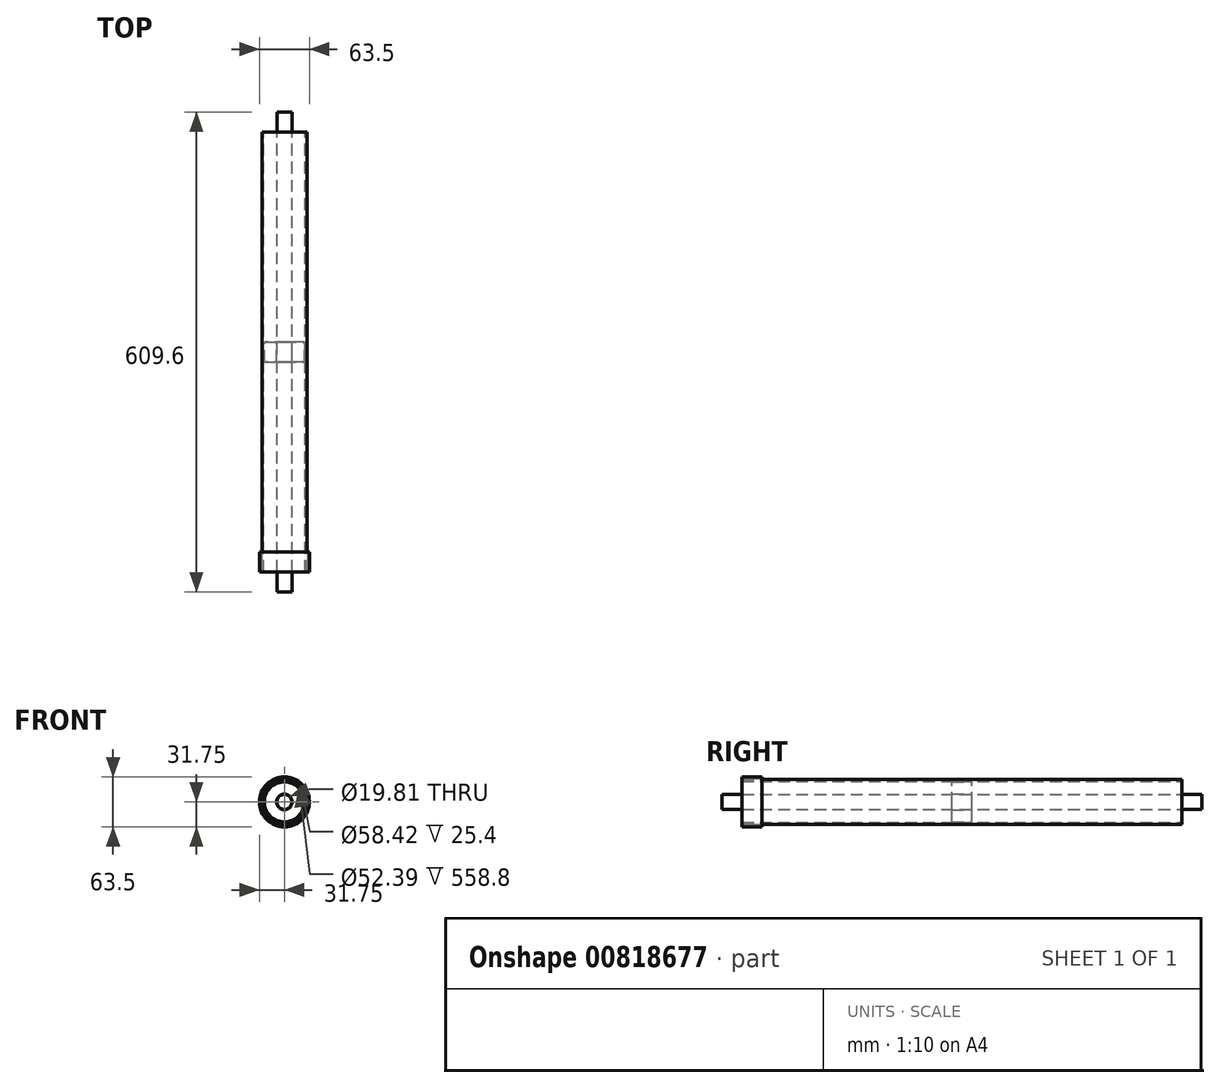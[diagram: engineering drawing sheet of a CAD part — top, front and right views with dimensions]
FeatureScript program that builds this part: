
annotation { "Feature Type Name" : "Feature", "Feature Type Description" : "" }
export const myFeature = defineFeature(function(context is Context, id is Id, definition is map)
    precondition{}
    {
        {
            var Q0;
            Q0=qCreatedBy(makeId("Front.planeOp"),FACE);
            var sketch = newSketch(context, id + "F0", { "sketchPlane" : qUnion([Q0])});
            skCircle(sketch, "E0", {"center": v(0, 0) * mm, "radius": 9.53 * mm});
            skSolve(sketch);
        }
        {
            var Q0;
            Q0 = qSketchRegion(id + "F0", true);
            extrude(context, id + "F1", {"entities" : qUnion([Q0]), "endBound" : BoundingType.SYMMETRIC, "depth" : 609.6 * mm, "offsetDistance" : 25.4 * mm});
        }
        {
            var Q0;
            Q0=qCreatedBy(makeId("Front.planeOp"),FACE);
            var sketch = newSketch(context, id + "F2", { "sketchPlane" : qUnion([Q0])});
            skCircle(sketch, "E1", {"center": v(0, 0) * mm, "radius": 25.4 * mm});
            skCircle(sketch, "E2", {"center": v(0, 0) * mm, "radius": 9.9 * mm});
            skSolve(sketch);
        }
        {
            var Q0;
            Q0 = qSketchRegion(id + "F2", true);
            extrude(context, id + "F3", {"entities" : qUnion([Q0]), "operationType" : NewBodyOperationType.ADD, "endBound" : BoundingType.SYMMETRIC, "depth" : 25.4 * mm, "offsetDistance" : 25.4 * mm});
        }
        {
            var Q0;
            Q0=qCreatedBy(makeId("Front.planeOp"),FACE);
            var sketch = newSketch(context, id + "F4", { "sketchPlane" : qUnion([Q0])});
            skCircle(sketch, "E3", {"center": v(0, 0) * mm, "radius": 26.2 * mm});
            skCircle(sketch, "E4", {"center": v(0, 0) * mm, "radius": 28.58 * mm});
            skSolve(sketch);
        }
        {
            var Q0;
            Q0 = qSketchRegion(id + "F4", true);
            extrude(context, id + "F5", {"entities" : qUnion([Q0]), "endBound" : BoundingType.SYMMETRIC, "depth" : 558.8 * mm, "offsetDistance" : 25.4 * mm});
        }
        {
            var Q0;
            Q0=makeQuery(id+"F5.opExtrude","CAP_FACE",FACE,{"disambiguationData":[OSD([sQuery(id+"F4.wireOp",EDGE,"E3"),sQuery(id+"F4.wireOp",EDGE,"E4")])],"isStart":false});
            var sketch = newSketch(context, id + "F6", { "sketchPlane" : qUnion([Q0])});
            skCircle(sketch, "E5", {"center": v(0, 0) * mm, "radius": 31.75 * mm});
            skCircle(sketch, "E6", {"center": v(0, 0) * mm, "radius": 10.16 * mm});
            skCircle(sketch, "E7", {"center": v(0, 0) * mm, "radius": 29.21 * mm});
            skSolve(sketch);
        }
        {
            var Q0;
            Q0 = qSketchRegion(id + "F6", true);
            extrude(context, id + "F7", {"entities" : qUnion([Q0]), "operationType" : NewBodyOperationType.ADD, "oppositeDirection" : true, "depth" : 25.4 * mm, "offsetDistance" : 25.4 * mm});
        }
    });
